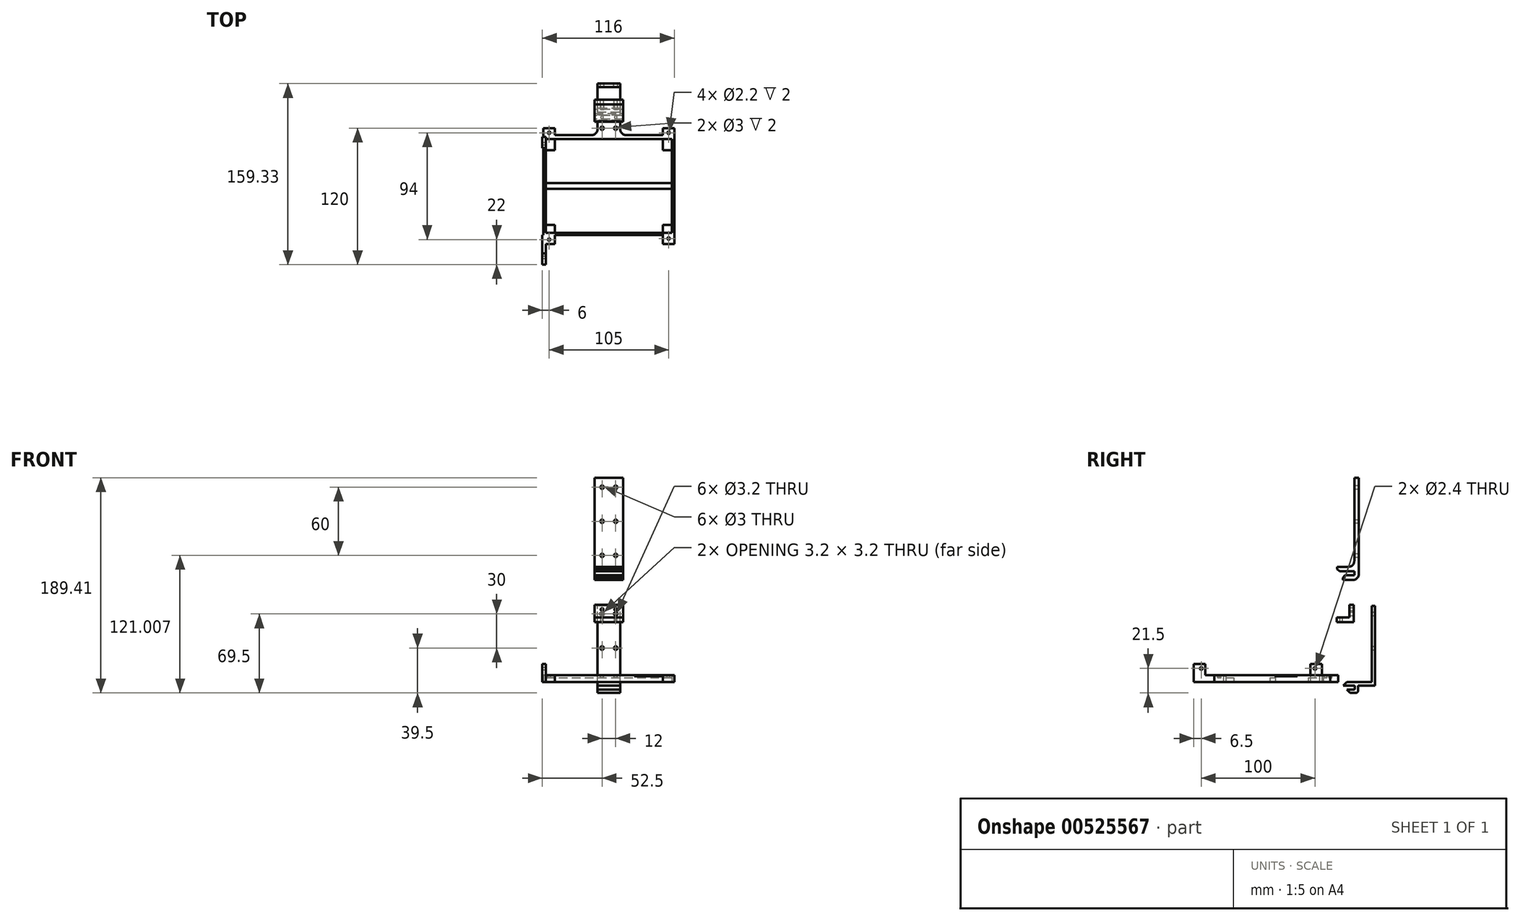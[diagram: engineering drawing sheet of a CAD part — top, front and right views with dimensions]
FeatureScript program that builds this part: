
annotation { "Feature Type Name" : "Feature", "Feature Type Description" : "" }
export const myFeature = defineFeature(function(context is Context, id is Id, definition is map)
    precondition{}
    {
        {
            var Q0;
            Q0=qCreatedBy(makeId("Top.planeOp"),FACE);
            var sketch = newSketch(context, id + "F0", { "sketchPlane" : qUnion([Q0])});
            skLineSegment(sketch, "E0.bottom", {"start": v(55.5, -41.25) * mm, "end": v(-55.5, -41.25) * mm});
            skLineSegment(sketch, "E0.top", {"start": v(55.5, 41.25) * mm, "end": v(-55.5, 41.25) * mm});
            skLineSegment(sketch, "E0.left", {"start": v(55.5, -41.25) * mm, "end": v(55.5, 41.25) * mm});
            skLineSegment(sketch, "E0.right", {"start": v(-55.5, -41.25) * mm, "end": v(-55.5, 41.25) * mm});
            skPoint(sketch, "E0.middle", {"position": v(0, 0) * mm});
            skLineSegment(sketch, "E1.bottom", {"start": v(57.5, -43.25) * mm, "end": v(-57.5, -43.25) * mm});
            skLineSegment(sketch, "E1.top", {"start": v(57.5, 43.25) * mm, "end": v(-57.5, 43.25) * mm});
            skLineSegment(sketch, "E1.left", {"start": v(57.5, -43.25) * mm, "end": v(57.5, 43.25) * mm});
            skLineSegment(sketch, "E1.right", {"start": v(-57.5, -43.25) * mm, "end": v(-57.5, 43.25) * mm});
            skSolve(sketch);
        }
        {
            var Q0;
            Q0=qSketchRegion(id+"F0",true);
            extrude(context, id + "F1", {"entities" : qUnion([Q0]), "depth" : 6 * mm, "offsetDistance" : 25 * mm});
        }
        {
            var Q0;
            Q0=makeQuery(id+"F1.opExtrude","CAP_FACE",FACE,{"disambiguationData":[OSD([sQuery(id+"F0.wireOp",EDGE,"E0.bottom"),sQuery(id+"F0.wireOp",EDGE,"E0.top"),sQuery(id+"F0.wireOp",EDGE,"E0.left"),sQuery(id+"F0.wireOp",EDGE,"E0.right"),sQuery(id+"F0.wireOp",EDGE,"E1.bottom"),sQuery(id+"F0.wireOp",EDGE,"E1.top"),sQuery(id+"F0.wireOp",EDGE,"E1.left"),sQuery(id+"F0.wireOp",EDGE,"E1.right")])],"isStart":true});
            var sketch = newSketch(context, id + "F2", { "sketchPlane" : qUnion([Q0])});
            skLineSegment(sketch, "E2.bottom", {"start": v(-55.5, -41.25) * mm, "end": v(-47.5, -41.25) * mm});
            skLineSegment(sketch, "E2.top", {"start": v(-55.5, -31.25) * mm, "end": v(-47.5, -31.25) * mm});
            skLineSegment(sketch, "E2.left", {"start": v(-55.5, -41.25) * mm, "end": v(-55.5, -31.25) * mm});
            skLineSegment(sketch, "E2.right", {"start": v(-47.5, -41.25) * mm, "end": v(-47.5, -31.25) * mm});
            skLineSegment(sketch, "E3.bottom", {"start": v(55.5, -41.25) * mm, "end": v(47.5, -41.25) * mm});
            skLineSegment(sketch, "E3.top", {"start": v(55.5, -31.25) * mm, "end": v(47.5, -31.25) * mm});
            skLineSegment(sketch, "E3.left", {"start": v(55.5, -41.25) * mm, "end": v(55.5, -31.25) * mm});
            skLineSegment(sketch, "E3.right", {"start": v(47.5, -41.25) * mm, "end": v(47.5, -31.25) * mm});
            skLineSegment(sketch, "E4.bottom", {"start": v(-55.5, 41.25) * mm, "end": v(-47.5, 41.25) * mm});
            skLineSegment(sketch, "E4.top", {"start": v(-55.5, 34.25) * mm, "end": v(-47.5, 34.25) * mm});
            skLineSegment(sketch, "E4.left", {"start": v(-55.5, 41.25) * mm, "end": v(-55.5, 34.25) * mm});
            skLineSegment(sketch, "E4.right", {"start": v(-47.5, 41.25) * mm, "end": v(-47.5, 34.25) * mm});
            skLineSegment(sketch, "E5.bottom", {"start": v(55.5, 41.25) * mm, "end": v(47.5, 41.25) * mm});
            skLineSegment(sketch, "E5.top", {"start": v(55.5, 34.25) * mm, "end": v(47.5, 34.25) * mm});
            skLineSegment(sketch, "E5.left", {"start": v(55.5, 41.25) * mm, "end": v(55.5, 34.25) * mm});
            skLineSegment(sketch, "E5.right", {"start": v(47.5, 41.25) * mm, "end": v(47.5, 34.25) * mm});
            skLineSegment(sketch, "E6.bottom", {"start": v(-55.5, -2.5) * mm, "end": v(55.5, -2.5) * mm});
            skLineSegment(sketch, "E6.top", {"start": v(-55.5, 2.5) * mm, "end": v(55.5, 2.5) * mm});
            skLineSegment(sketch, "E6.left", {"start": v(-55.5, -2.5) * mm, "end": v(-55.5, 2.5) * mm});
            skLineSegment(sketch, "E6.right", {"start": v(55.5, -2.5) * mm, "end": v(55.5, 2.5) * mm});
            skSolve(sketch);
        }
        {
            var Q0;
            Q0=qSketchRegion(id+"F2",true);
            extrude(context, id + "F3", {"entities" : qUnion([Q0]), "operationType" : NewBodyOperationType.ADD, "oppositeDirection" : true, "depth" : 4 * mm, "offsetDistance" : 25 * mm});
        }
        {
            var Q0;
            Q0=makeQuery(id+"F1.opExtrude","CAP_FACE",FACE,{"disambiguationData":[OSD([sQuery(id+"F0.wireOp",EDGE,"E0.bottom"),sQuery(id+"F0.wireOp",EDGE,"E0.top"),sQuery(id+"F0.wireOp",EDGE,"E0.left"),sQuery(id+"F0.wireOp",EDGE,"E0.right"),sQuery(id+"F0.wireOp",EDGE,"E1.bottom"),sQuery(id+"F0.wireOp",EDGE,"E1.top"),sQuery(id+"F0.wireOp",EDGE,"E1.left"),sQuery(id+"F0.wireOp",EDGE,"E1.right")])],"isStart":false});
            var sketch = newSketch(context, id + "F4", { "sketchPlane" : qUnion([Q0])});
            skLineSegment(sketch, "E7.bottom", {"start": v(22.5, -41.25) * mm, "end": v(47.5, -41.25) * mm});
            skLineSegment(sketch, "E7.top", {"start": v(22.5, -43.25) * mm, "end": v(47.5, -43.25) * mm});
            skLineSegment(sketch, "E7.left", {"start": v(22.5, -41.25) * mm, "end": v(22.5, -43.25) * mm});
            skLineSegment(sketch, "E7.right", {"start": v(47.5, -41.25) * mm, "end": v(47.5, -43.25) * mm});
            skLineSegment(sketch, "E8.bottom", {"start": v(57.5, 21.75) * mm, "end": v(55.5, 21.75) * mm});
            skLineSegment(sketch, "E8.top", {"start": v(57.5, 1.75) * mm, "end": v(55.5, 1.75) * mm});
            skLineSegment(sketch, "E8.left", {"start": v(57.5, 21.75) * mm, "end": v(57.5, 1.75) * mm});
            skLineSegment(sketch, "E8.right", {"start": v(55.5, 21.75) * mm, "end": v(55.5, 1.75) * mm});
            skSolve(sketch);
        }
        {
            var Q0;
            Q0=qSketchRegion(id+"F4",true);
            extrude(context, id + "F5", {"entities" : qUnion([Q0]), "operationType" : NewBodyOperationType.REMOVE, "oppositeDirection" : true, "depth" : 1 * mm, "offsetDistance" : 25 * mm});
        }
        {
            var Q0;
            Q0=makeQuery(id+"F3.boolean.opBoolean","MERGE",FACE,{"derivedFrom":[makeQuery(id+"F1.opExtrude","CAP_FACE",FACE,{"disambiguationData":[OSD([sQuery(id+"F0.wireOp",EDGE,"E0.bottom"),sQuery(id+"F0.wireOp",EDGE,"E0.top"),sQuery(id+"F0.wireOp",EDGE,"E0.left"),sQuery(id+"F0.wireOp",EDGE,"E0.right"),sQuery(id+"F0.wireOp",EDGE,"E1.bottom"),sQuery(id+"F0.wireOp",EDGE,"E1.top"),sQuery(id+"F0.wireOp",EDGE,"E1.left"),sQuery(id+"F0.wireOp",EDGE,"E1.right")])],"isStart":true}),makeQuery(id+"F3.opExtrude","CAP_FACE",FACE,{"disambiguationData":[OSD([sQuery(id+"F2.wireOp",EDGE,"E2.bottom"),sQuery(id+"F2.wireOp",EDGE,"E2.top"),sQuery(id+"F2.wireOp",EDGE,"E2.left"),sQuery(id+"F2.wireOp",EDGE,"E2.right")])],"isStart":true}),makeQuery(id+"F3.opExtrude","CAP_FACE",FACE,{"disambiguationData":[OSD([sQuery(id+"F2.wireOp",EDGE,"E3.bottom"),sQuery(id+"F2.wireOp",EDGE,"E3.top"),sQuery(id+"F2.wireOp",EDGE,"E3.left"),sQuery(id+"F2.wireOp",EDGE,"E3.right")])],"isStart":true}),makeQuery(id+"F3.opExtrude","CAP_FACE",FACE,{"disambiguationData":[OSD([sQuery(id+"F2.wireOp",EDGE,"E4.bottom"),sQuery(id+"F2.wireOp",EDGE,"E4.top"),sQuery(id+"F2.wireOp",EDGE,"E4.left"),sQuery(id+"F2.wireOp",EDGE,"E4.right")])],"isStart":true}),makeQuery(id+"F3.opExtrude","CAP_FACE",FACE,{"disambiguationData":[OSD([sQuery(id+"F2.wireOp",EDGE,"E5.bottom"),sQuery(id+"F2.wireOp",EDGE,"E5.top"),sQuery(id+"F2.wireOp",EDGE,"E5.left"),sQuery(id+"F2.wireOp",EDGE,"E5.right")])],"isStart":true})]});
            var sketch = newSketch(context, id + "F6", { "sketchPlane" : qUnion([Q0])});
            skLineSegment(sketch, "E9.bottom", {"start": v(10, -57.75) * mm, "end": v(-10, -57.75) * mm});
            skLineSegment(sketch, "E9.top", {"start": v(10, -44.75) * mm, "end": v(-10, -44.75) * mm});
            skLineSegment(sketch, "E9.left", {"start": v(10, -57.75) * mm, "end": v(10, -44.75) * mm});
            skLineSegment(sketch, "E9.right", {"start": v(-10, -57.75) * mm, "end": v(-10, -44.75) * mm});
            skPoint(sketch, "E9.middle", {"position": v(0, -51.25) * mm});
            skCircle(sketch, "E10", {"center": v(-6, -50.75) * mm, "radius": 1.5 * mm, "construction": true});
            skCircle(sketch, "E11", {"center": v(6, -50.75) * mm, "radius": 1.5 * mm, "construction": true});
            skLineSegment(sketch, "E12.bottom", {"start": v(-57.5, -43.25) * mm, "end": v(57.5, -43.25) * mm});
            skLineSegment(sketch, "E12.top", {"start": v(-57.5, -44.75) * mm, "end": v(57.5, -44.75) * mm});
            skLineSegment(sketch, "E12.left", {"start": v(-57.5, -43.25) * mm, "end": v(-57.5, -44.75) * mm});
            skLineSegment(sketch, "E12.right", {"start": v(57.5, -43.25) * mm, "end": v(57.5, -44.75) * mm});
            skSolve(sketch);
        }
        {
            var Q0;
            Q0 = qSketchRegion(id + "F6", true);
            extrude(context, id + "F7", {"entities" : qUnion([Q0]), "operationType" : NewBodyOperationType.ADD, "oppositeDirection" : true, "depth" : 6 * mm, "offsetDistance" : 25 * mm});
        }
        {
            var Q0;
            Q0=qCreatedBy(makeId("Top.planeOp"),FACE);
            var sketch = newSketch(context, id + "F8", { "sketchPlane" : qUnion([Q0])});
            skLineSegment(sketch, "E13.bottom", {"start": v(10, 75.08) * mm, "end": v(-10, 75.08) * mm});
            skLineSegment(sketch, "E13.top", {"start": v(10, 87.08) * mm, "end": v(-10, 87.08) * mm});
            skLineSegment(sketch, "E13.left", {"start": v(10, 75.08) * mm, "end": v(10, 87.08) * mm});
            skLineSegment(sketch, "E13.right", {"start": v(-10, 75.08) * mm, "end": v(-10, 87.08) * mm});
            skPoint(sketch, "E13.middle", {"position": v(0, 81.08) * mm});
            skCircle(sketch, "E14", {"center": v(-6, 81.08) * mm, "radius": 1.2 * mm, "construction": true});
            skCircle(sketch, "E15", {"center": v(6, 81.08) * mm, "radius": 1.2 * mm, "construction": true});
            skSolve(sketch);
        }
        {
            var Q0;
            Q0 = qSketchRegion(id + "F8", true);
            extrude(context, id + "F9", {"entities" : qUnion([Q0]), "oppositeDirection" : true, "depth" : 3 * mm, "offsetDistance" : 25 * mm});
        }
        {
            var Q0;
            Q0=makeQuery(id+"F9.opExtrude","SWEPT_FACE",FACE,{"disambiguationData":[OSD([sQuery(id+"F8.wireOp",EDGE,"E13.right")])]});
            var sketch = newSketch(context, id + "F10", { "sketchPlane" : qUnion([Q0])});
            skLineSegment(sketch, "E16", {"start": v(-75.08, -3) * mm, "end": v(-75.08, -9.5) * mm});
            skLineSegment(sketch, "E17", {"start": v(-75.08, -9.5) * mm, "end": v(-65.08, -9.5) * mm});
            skLineSegment(sketch, "E18", {"start": v(-65.08, -9.5) * mm, "end": v(-65.08, -6.5) * mm});
            skLineSegment(sketch, "E19", {"start": v(-65.08, -6.5) * mm, "end": v(-71.58, -6.5) * mm});
            skLineSegment(sketch, "E20", {"start": v(-72.08, -6) * mm, "end": v(-72.08, -3.5) * mm});
            skLineSegment(sketch, "E21", {"start": v(-71.58, -3) * mm, "end": v(-62.08, -3) * mm});
            skLineSegment(sketch, "E22", {"start": v(-62.08, -3) * mm, "end": v(-62.08, 0) * mm});
            skLineSegment(sketch, "E23", {"start": v(-62.08, 0) * mm, "end": v(-75.08, 0) * mm});
            skLineSegment(sketch, "E24", {"start": v(-75.08, 0) * mm, "end": v(-75.08, -3) * mm});
            skPoint(sketch, "E25.visualSharp", {"position": v(-72.08, -3) * mm});
            skArc(sketch, "E25.filletArc", {"start": v(-71.58, -3) * mm, "mid": v(-71.94, -3.15) * mm, "end": v(-72.08, -3.5) * mm});
            skPoint(sketch, "E26.visualSharp", {"position": v(-72.08, -6.5) * mm});
            skArc(sketch, "E26.filletArc", {"start": v(-72.08, -6) * mm, "mid": v(-71.94, -6.35) * mm, "end": v(-71.58, -6.5) * mm});
            skLineSegment(sketch, "E27.bottom", {"start": v(-87.08, -3) * mm, "end": v(-90.08, -3) * mm});
            skLineSegment(sketch, "E27.top", {"start": v(-87.08, 67) * mm, "end": v(-90.08, 67) * mm});
            skLineSegment(sketch, "E27.left", {"start": v(-87.08, -3) * mm, "end": v(-87.08, 67) * mm});
            skLineSegment(sketch, "E27.right", {"start": v(-90.08, -3) * mm, "end": v(-90.08, 67) * mm});
            skSolve(sketch);
        }
        {
            var Q0;
            Q0 = qSketchRegion(id + "F10", true);
            extrude(context, id + "F11", {"entities" : qUnion([Q0]), "operationType" : NewBodyOperationType.ADD, "oppositeDirection" : true, "depth" : 20 * mm, "offsetDistance" : 25 * mm});
        }
        {
            var Q0;
            Q0=qCreatedBy(makeId("Top.planeOp"),FACE);
            var sketch = newSketch(context, id + "F12", { "sketchPlane" : qUnion([Q0])});
            skLineSegment(sketch, "E28.bottom", {"start": v(-58.5, 43.25) * mm, "end": v(-55.5, 43.25) * mm});
            skLineSegment(sketch, "E28.top", {"start": v(-58.5, 33.25) * mm, "end": v(-55.5, 33.25) * mm});
            skLineSegment(sketch, "E28.left", {"start": v(-58.5, 43.25) * mm, "end": v(-58.5, 33.25) * mm});
            skLineSegment(sketch, "E28.right", {"start": v(-55.5, 43.25) * mm, "end": v(-55.5, 33.25) * mm});
            skLineSegment(sketch, "E29.bottom", {"start": v(-55.5, -43.25) * mm, "end": v(-58.5, -43.25) * mm});
            skLineSegment(sketch, "E29.top", {"start": v(-55.5, -69.25) * mm, "end": v(-58.5, -69.25) * mm});
            skLineSegment(sketch, "E29.left", {"start": v(-55.5, -43.25) * mm, "end": v(-55.5, -69.25) * mm});
            skLineSegment(sketch, "E29.right", {"start": v(-58.5, -43.25) * mm, "end": v(-58.5, -69.25) * mm});
            skSolve(sketch);
        }
        {
            var Q0;
            Q0 = qSketchRegion(id + "F12", true);
            extrude(context, id + "F13", {"entities" : qUnion([Q0]), "operationType" : NewBodyOperationType.ADD, "depth" : 16 * mm, "offsetDistance" : 25 * mm});
        }
        {
            var Q0;
            Q0=makeQuery(id+"F11.opExtrude","SWEPT_EDGE",EDGE,{"disambiguationData":[OSD([sQuery(id+"F10.wireOp",EDGE,"E22"),sQuery(id+"F10.wireOp",EDGE,"E23")])]});
            var Q1;
            Q1=makeQuery(id+"F11.opExtrude","SWEPT_EDGE",EDGE,{"disambiguationData":[OSD([sQuery(id+"F10.wireOp",EDGE,"E17"),sQuery(id+"F10.wireOp",EDGE,"E18")])]});
            chamfer(context, id + "F14", {"entities" : qUnion([Q0, Q1]), "width" : 3 * mm, "tangentPropagation" : true});
        }
        {
            var Q0;
            Q0=makeQuery(id+"F13.opExtrude","SWEPT_FACE",FACE,{"disambiguationData":[OSD([sQuery(id+"F12.wireOp",EDGE,"E29.left")])]});
            var sketch = newSketch(context, id + "F15", { "sketchPlane" : qUnion([Q0])});
            skLineSegment(sketch, "E30.bottom", {"start": v(-43.25, 16) * mm, "end": v(-59.25, 16) * mm});
            skLineSegment(sketch, "E30.top", {"start": v(-43.25, 6) * mm, "end": v(-59.25, 6) * mm});
            skLineSegment(sketch, "E30.left", {"start": v(-43.25, 16) * mm, "end": v(-43.25, 6) * mm});
            skLineSegment(sketch, "E30.right", {"start": v(-59.25, 16) * mm, "end": v(-59.25, 6) * mm});
            skCircle(sketch, "E31", {"center": v(-62.75, 12) * mm, "radius": 1.2 * mm});
            skCircle(sketch, "E32", {"center": v(37.25, 12) * mm, "radius": 1.2 * mm});
            skSolve(sketch);
        }
        {
            var Q0;
            Q0 = qSketchRegion(id + "F15", true);
            extrude(context, id + "F16", {"entities" : qUnion([Q0]), "operationType" : NewBodyOperationType.REMOVE, "oppositeDirection" : true, "depth" : 25 * mm, "offsetDistance" : 25 * mm});
        }
        {
            var Q0;
            Q0=makeQuery(id+"F9.opExtrude","CAP_EDGE",EDGE,{"disambiguationData":[OSD([sQuery(id+"F8.wireOp",EDGE,"E13.bottom")])],"isStart":false});
            var Q1;
            Q1=makeQuery(id+"F11.opExtrude","SWEPT_EDGE",EDGE,{"disambiguationData":[OSD([sQuery(id+"F10.wireOp",EDGE,"E16"),sQuery(id+"F10.wireOp",EDGE,"E17")])]});
            fillet(context, id + "F17", {"entities" : qUnion([Q0, Q1]), "radius" : 2 * mm, "tangentPropagation" : true, "allowEdgeOverflow" : false});
        }
        {
            var Q0;
            Q0=qCreatedBy(makeId("Right.planeOp"),FACE);
            var sketch = newSketch(context, id + "F18", { "sketchPlane" : qUnion([Q0])});
            skLineSegment(sketch, "E33.bottom", {"start": v(56.38, 56.93) * mm, "end": v(71.38, 56.93) * mm});
            skLineSegment(sketch, "E33.top", {"start": v(56.38, 52.93) * mm, "end": v(71.38, 52.93) * mm});
            skLineSegment(sketch, "E33.left", {"start": v(56.38, 56.93) * mm, "end": v(56.38, 52.93) * mm});
            skLineSegment(sketch, "E33.right", {"start": v(71.38, 56.93) * mm, "end": v(71.38, 52.93) * mm});
            skLineSegment(sketch, "E34.bottom", {"start": v(71.38, 56.93) * mm, "end": v(67.38, 56.93) * mm});
            skLineSegment(sketch, "E34.top", {"start": v(71.38, 67.93) * mm, "end": v(67.38, 67.93) * mm});
            skLineSegment(sketch, "E34.left", {"start": v(71.38, 56.93) * mm, "end": v(71.38, 67.93) * mm});
            skLineSegment(sketch, "E34.right", {"start": v(67.38, 56.93) * mm, "end": v(67.38, 67.93) * mm});
            skSolve(sketch);
        }
        {
            var Q0;
            Q0 = qSketchRegion(id + "F18", true);
            extrude(context, id + "F19", {"entities" : qUnion([Q0]), "endBound" : BoundingType.SYMMETRIC, "depth" : 25 * mm, "offsetDistance" : 25 * mm});
        }
        {
            var Q0;
            Q0=makeQuery(id+"F19.opExtrude","SWEPT_FACE",FACE,{"disambiguationData":[OSD([sQuery(id+"F18.wireOp",EDGE,"E33.bottom")])]});
            var sketch = newSketch(context, id + "F20", { "sketchPlane" : qUnion([Q0])});
            skCircle(sketch, "E35", {"center": v(-6, 60.38) * mm, "radius": 1.2 * mm});
            skCircle(sketch, "E36", {"center": v(6, 60.38) * mm, "radius": 1.2 * mm});
            skSolve(sketch);
        }
        {
            var Q0;
            Q0=makeQuery(id+"F19.opExtrude","SWEPT_FACE",FACE,{"disambiguationData":[OSD([sQuery(id+"F18.wireOp",EDGE,"E34.right")])]});
            var sketch = newSketch(context, id + "F21", { "sketchPlane" : qUnion([Q0])});
            skCircle(sketch, "E37", {"center": v(-6, 63.93) * mm, "radius": 1.2 * mm});
            skCircle(sketch, "E38", {"center": v(6, 63.93) * mm, "radius": 1.2 * mm});
            skSolve(sketch);
        }
        {
            var Q0;
            Q0=sQuery(id+"F20.wireOp",VERTEX,"E35.center");
            var Q1;
            Q1=sQuery(id+"F20.wireOp",VERTEX,"E36.center");
            var Q2;
            Q2=sQuery(id+"F21.wireOp",VERTEX,"E37.center");
            var Q3;
            Q3=sQuery(id+"F21.wireOp",VERTEX,"E38.center");
            var Q4;
            Q4=makeQuery(id+"F19.opExtrude","SWEPT_BODY",BODY,{"disambiguationData":[OSD([sQuery(id+"F18.wireOp",EDGE,"E33.bottom"),sQuery(id+"F18.wireOp",EDGE,"E33.top"),sQuery(id+"F18.wireOp",EDGE,"E33.left"),sQuery(id+"F18.wireOp",EDGE,"E33.right"),sQuery(id+"F18.wireOp",EDGE,"E34.top"),sQuery(id+"F18.wireOp",EDGE,"E34.left"),sQuery(id+"F18.wireOp",EDGE,"E34.right")])]});
            hole(context, id + "F22", {"style" : HoleStyle.SIMPLE, "endStyle" : HoleEndStyle.BLIND, "holeDiameter" : 2.4 * mm, "majorDiameter" : 5 * mm, "holeDepth" : 5 * mm, "tappedDepth" : 12 * mm, "tapClearance" : 3, "locations" : qUnion([Q0, Q1, Q2, Q3]), "scope" : qUnion([Q4])});
        }
        {
            var Q0;
            Q0=makeQuery(id+"F11.opExtrude","SWEPT_FACE",FACE,{"disambiguationData":[OSD([sQuery(id+"F10.wireOp",EDGE,"E27.right")])]});
            var sketch = newSketch(context, id + "F23", { "sketchPlane" : qUnion([Q0])});
            skCircle(sketch, "E39", {"center": v(-6, 30) * mm, "radius": 1.6 * mm});
            skCircle(sketch, "E40", {"center": v(6, 30) * mm, "radius": 1.6 * mm});
            skCircle(sketch, "E41", {"center": v(-6, 60) * mm, "radius": 1.6 * mm});
            skCircle(sketch, "E42", {"center": v(6, 60) * mm, "radius": 1.6 * mm});
            skSolve(sketch);
        }
        {
            var Q0;
            Q0 = qSketchRegion(id + "F23", true);
            extrude(context, id + "F24", {"entities" : qUnion([Q0]), "operationType" : NewBodyOperationType.REMOVE, "oppositeDirection" : true, "depth" : 25 * mm, "offsetDistance" : 25 * mm});
        }
        {
            var Q0;
            Q0=qCreatedBy(makeId("Right.planeOp"),FACE);
            var sketch = newSketch(context, id + "F25", { "sketchPlane" : qUnion([Q0])});
            skLineSegment(sketch, "E43", {"start": v(61.75, 89.9) * mm, "end": v(75.75, 89.9) * mm});
            skLineSegment(sketch, "E44", {"start": v(75.75, 89.9) * mm, "end": v(75.75, 179.9) * mm});
            skLineSegment(sketch, "E45", {"start": v(75.75, 179.9) * mm, "end": v(71.75, 179.9) * mm});
            skLineSegment(sketch, "E46", {"start": v(71.75, 179.9) * mm, "end": v(71.75, 101.5) * mm});
            skLineSegment(sketch, "E47", {"start": v(71.75, 101.5) * mm, "end": v(56.75, 101.5) * mm});
            skLineSegment(sketch, "E48", {"start": v(56.75, 101.5) * mm, "end": v(56.75, 97.5) * mm});
            skLineSegment(sketch, "E49", {"start": v(56.75, 97.5) * mm, "end": v(71.75, 97.5) * mm});
            skLineSegment(sketch, "E50", {"start": v(71.75, 97.5) * mm, "end": v(71.75, 93.9) * mm});
            skLineSegment(sketch, "E51", {"start": v(71.75, 93.9) * mm, "end": v(61.75, 93.9) * mm});
            skLineSegment(sketch, "E52", {"start": v(61.75, 93.9) * mm, "end": v(61.75, 89.9) * mm});
            skSolve(sketch);
        }
        {
            var Q0;
            Q0 = qSketchRegion(id + "F25", true);
            extrude(context, id + "F26", {"entities" : qUnion([Q0]), "endBound" : BoundingType.SYMMETRIC, "depth" : 25 * mm, "offsetDistance" : 25 * mm});
        }
        {
            var Q0;
            Q0=makeQuery(id+"F26.opExtrude","SWEPT_EDGE",EDGE,{"disambiguationData":[OSD([sQuery(id+"F25.wireOp",EDGE,"E46"),sQuery(id+"F25.wireOp",EDGE,"E47")])]});
            var Q1;
            Q1=makeQuery(id+"F26.opExtrude","SWEPT_EDGE",EDGE,{"disambiguationData":[OSD([sQuery(id+"F25.wireOp",EDGE,"E43"),sQuery(id+"F25.wireOp",EDGE,"E44")])]});
            var Q2;
            Q2=makeQuery(id+"F7.opExtrude","SWEPT_EDGE",EDGE,{"disambiguationData":[OSD([sQuery(id+"F6.wireOp",EDGE,"E9.right"),sQuery(id+"F6.wireOp",EDGE,"E12.top")])]});
            var Q3;
            Q3=makeQuery(id+"F7.opExtrude","SWEPT_EDGE",EDGE,{"disambiguationData":[OSD([sQuery(id+"F6.wireOp",EDGE,"E9.left"),sQuery(id+"F6.wireOp",EDGE,"E12.top")])]});
            fillet(context, id + "F27", {"entities" : qUnion([Q0, Q1, Q2, Q3]), "radius" : 5 * mm, "tangentPropagation" : true, "allowEdgeOverflow" : false});
        }
        {
            var Q0;
            Q0=makeQuery(id+"F26.opExtrude","SWEPT_EDGE",EDGE,{"disambiguationData":[OSD([sQuery(id+"F25.wireOp",EDGE,"E48"),sQuery(id+"F25.wireOp",EDGE,"E49")])]});
            var Q1;
            Q1=makeQuery(id+"F26.opExtrude","SWEPT_EDGE",EDGE,{"disambiguationData":[OSD([sQuery(id+"F25.wireOp",EDGE,"E51"),sQuery(id+"F25.wireOp",EDGE,"E52")])]});
            chamfer(context, id + "F28", {"entities" : qUnion([Q0, Q1]), "width" : 2 * mm, "tangentPropagation" : true});
        }
        {
            var Q0;
            Q0=makeQuery(id+"F26.opExtrude","SWEPT_FACE",FACE,{"disambiguationData":[OSD([sQuery(id+"F25.wireOp",EDGE,"E44")])]});
            var sketch = newSketch(context, id + "F29", { "sketchPlane" : qUnion([Q0])});
            skCircle(sketch, "E53", {"center": v(6, 111.5) * mm, "radius": 1.5 * mm});
            skCircle(sketch, "E54", {"center": v(-6, 111.5) * mm, "radius": 1.5 * mm});
            skCircle(sketch, "E55.0.1.0", {"center": v(6, 141.5) * mm, "radius": 1.5 * mm});
            skCircle(sketch, "E55.0.1.1", {"center": v(-6, 141.5) * mm, "radius": 1.5 * mm});
            skCircle(sketch, "E55.0.2.0", {"center": v(6, 171.5) * mm, "radius": 1.5 * mm});
            skCircle(sketch, "E55.0.2.1", {"center": v(-6, 171.5) * mm, "radius": 1.5 * mm});
            skLineSegment(sketch, "E55.direction1", {"start": v(-6, 111.5) * mm, "end": v(19, 111.5) * mm, "construction": true});
            skLineSegment(sketch, "E55.direction2", {"start": v(-6, 111.5) * mm, "end": v(-6, 141.5) * mm, "construction": true});
            skSolve(sketch);
        }
        {
            var Q0;
            Q0 = qSketchRegion(id + "F29", true);
            extrude(context, id + "F30", {"entities" : qUnion([Q0]), "operationType" : NewBodyOperationType.REMOVE, "oppositeDirection" : true, "depth" : 25 * mm, "offsetDistance" : 25 * mm});
        }
        {
            var Q0;
            Q0=qCreatedBy(makeId("Top.planeOp"),FACE);
            var sketch = newSketch(context, id + "F31", { "sketchPlane" : qUnion([Q0])});
            skLineSegment(sketch, "E56.3", {"start": v(-57.5, 44.75) * mm, "end": v(-15, 44.75) * mm});
            skLineSegment(sketch, "E56.4", {"start": v(15, 44.75) * mm, "end": v(57.5, 44.75) * mm});
            skLineSegment(sketch, "E57.bottom", {"start": v(57.5, -43.25) * mm, "end": v(47.5, -43.25) * mm});
            skLineSegment(sketch, "E57.top", {"start": v(57.5, -51.25) * mm, "end": v(47.5, -51.25) * mm});
            skLineSegment(sketch, "E57.left", {"start": v(57.5, -43.25) * mm, "end": v(57.5, -51.25) * mm});
            skLineSegment(sketch, "E57.right", {"start": v(47.5, -43.25) * mm, "end": v(47.5, -51.25) * mm});
            skLineSegment(sketch, "E58.0", {"start": v(57.5, -43.25) * mm, "end": v(-55.5, -43.25) * mm});
            skLineSegment(sketch, "E58.1", {"start": v(-55.5, -43.25) * mm, "end": v(-55.5, -69.25) * mm});
            skLineSegment(sketch, "E59.bottom", {"start": v(-55.5, -43.25) * mm, "end": v(-47.5, -43.25) * mm});
            skLineSegment(sketch, "E59.top", {"start": v(-55.5, -51.25) * mm, "end": v(-47.5, -51.25) * mm});
            skLineSegment(sketch, "E59.left", {"start": v(-55.5, -43.25) * mm, "end": v(-55.5, -51.25) * mm});
            skLineSegment(sketch, "E59.right", {"start": v(-47.5, -43.25) * mm, "end": v(-47.5, -51.25) * mm});
            skLineSegment(sketch, "E60.bottom", {"start": v(-57.5, 44.75) * mm, "end": v(-47.5, 44.75) * mm});
            skLineSegment(sketch, "E60.top", {"start": v(-57.5, 50.75) * mm, "end": v(-47.5, 50.75) * mm});
            skLineSegment(sketch, "E60.left", {"start": v(-57.5, 44.75) * mm, "end": v(-57.5, 50.75) * mm});
            skLineSegment(sketch, "E60.right", {"start": v(-47.5, 44.75) * mm, "end": v(-47.5, 50.75) * mm});
            skLineSegment(sketch, "E61.bottom", {"start": v(57.5, 44.75) * mm, "end": v(47.5, 44.75) * mm});
            skLineSegment(sketch, "E61.top", {"start": v(57.5, 50.75) * mm, "end": v(47.5, 50.75) * mm});
            skLineSegment(sketch, "E61.left", {"start": v(57.5, 44.75) * mm, "end": v(57.5, 50.75) * mm});
            skLineSegment(sketch, "E61.right", {"start": v(47.5, 44.75) * mm, "end": v(47.5, 50.75) * mm});
            skPoint(sketch, "E62", {"position": v(52.5, -47.25) * mm});
            skPoint(sketch, "E62.positionSnap0", {"position": v(52.5, -43.25) * mm});
            skPoint(sketch, "E62.positionSnap1", {"position": v(47.5, -47.25) * mm});
            skPoint(sketch, "E63", {"position": v(-51.5, -47.25) * mm});
            skPoint(sketch, "E63.positionSnap0", {"position": v(-47.5, -47.25) * mm});
            skPoint(sketch, "E63.positionSnap1", {"position": v(-51.5, -43.25) * mm});
            skPoint(sketch, "E64", {"position": v(-52.5, 46.75) * mm});
            skPoint(sketch, "E64.positionSnap0", {"position": v(-52.5, 50.75) * mm});
            skPoint(sketch, "E65", {"position": v(52.5, 46.75) * mm});
            skPoint(sketch, "E65.positionSnap0", {"position": v(52.5, 50.75) * mm});
            skSolve(sketch);
        }
        {
            var Q0;
            Q0 = qSketchRegion(id + "F31", true);
            extrude(context, id + "F32", {"entities" : qUnion([Q0]), "operationType" : NewBodyOperationType.ADD, "depth" : 6 * mm, "offsetDistance" : 25 * mm});
        }
        {
            var Q0;
            {var subQ0=sQuery(id+"F6.wireOp",EDGE,"E9.bottom");var subQ2=sQuery(id+"F0.wireOp",EDGE,"E1.right");var subQ4=sQuery(id+"F6.wireOp",EDGE,"E9.left");var subQ5=sQuery(id+"F0.wireOp",EDGE,"E0.top");var subQ6=makeQuery(id+"F1.opExtrude","SWEPT_FACE",FACE,{"disambiguationData":[OSD([subQ5])]});var subQ7=sQuery(id+"F0.wireOp",EDGE,"E1.left");var subQ9=sQuery(id+"F6.wireOp",EDGE,"E9.right");var subQ10=sQuery(id+"F0.wireOp",EDGE,"E0.left");var subQ12=sQuery(id+"F6.wireOp",EDGE,"E10");var subQ13=sQuery(id+"F0.wireOp",EDGE,"E0.right");var subQ15=sQuery(id+"F6.wireOp",EDGE,"E11");var subQ16=sQuery(id+"F6.wireOp",EDGE,"E12.top");var subQ17=sQuery(id+"F6.wireOp",EDGE,"E12.left");var subQ18=sQuery(id+"F6.wireOp",EDGE,"E12.right");var subQ19=sQuery(id+"F0.wireOp",EDGE,"E0.bottom");var subQ20=sQuery(id+"F0.wireOp",EDGE,"E1.bottom");var subQ21=sQuery(id+"F0.wireOp",EDGE,"E1.top");Q0=makeQuery(id+"F32.boolean.opBoolean","MERGE",FACE,{"derivedFrom":[makeQuery(id+"F13.boolean.opBoolean","SPLIT",FACE,{"disambiguationData":[TD([subQ6])],"derivedFrom":makeQuery(id+"F7.boolean.opBoolean","MERGE",FACE,{"derivedFrom":[makeQuery(id+"F5.boolean.opBoolean","SPLIT",FACE,{"disambiguationData":[TD([subQ6])],"derivedFrom":makeQuery(id+"F1.opExtrude","CAP_FACE",FACE,{"disambiguationData":[OSD([subQ19,subQ5,subQ10,subQ13,subQ20,subQ21,subQ7,subQ2])],"isStart":false})}),makeQuery(id+"F7.opExtrude","CAP_FACE",FACE,{"disambiguationData":[OSD([subQ0,subQ4,subQ9,subQ12,subQ15,sQuery(id+"F6.wireOp",EDGE,"E12.bottom"),subQ16,subQ17,subQ18])],"isStart":false})]})}),makeQuery(id+"F32.opExtrude","CAP_FACE",FACE,{"disambiguationData":[OSD([sQuery(id+"F31.wireOp",EDGE,"E60.bottom"),sQuery(id+"F31.wireOp",EDGE,"E60.top"),sQuery(id+"F31.wireOp",EDGE,"E60.left"),sQuery(id+"F31.wireOp",EDGE,"E60.right")])],"isStart":false}),makeQuery(id+"F32.opExtrude","CAP_FACE",FACE,{"disambiguationData":[OSD([sQuery(id+"F31.wireOp",EDGE,"E61.bottom"),sQuery(id+"F31.wireOp",EDGE,"E61.top"),sQuery(id+"F31.wireOp",EDGE,"E61.left"),sQuery(id+"F31.wireOp",EDGE,"E61.right")])],"isStart":false})]});}
            var sketch = newSketch(context, id + "F33", { "sketchPlane" : qUnion([Q0])});
            skCircle(sketch, "E66", {"center": v(-52.5, 46.75) * mm, "radius": 1.1 * mm});
            skPoint(sketch, "E66.centerSnap0", {"position": v(-52.5, 50.75) * mm});
            skCircle(sketch, "E67", {"center": v(52.5, 46.75) * mm, "radius": 1.1 * mm});
            skPoint(sketch, "E67.centerSnap0", {"position": v(52.5, 50.75) * mm});
            skLineSegment(sketch, "E68.0", {"start": v(-55.5, -51.25) * mm, "end": v(-47.5, -51.25) * mm});
            skLineSegment(sketch, "E68.1", {"start": v(-47.5, -43.25) * mm, "end": v(-47.5, -51.25) * mm});
            skLineSegment(sketch, "E68.2", {"start": v(57.5, -51.25) * mm, "end": v(47.5, -51.25) * mm});
            skLineSegment(sketch, "E68.3", {"start": v(47.5, -41.25) * mm, "end": v(47.5, -51.25) * mm});
            skCircle(sketch, "E69", {"center": v(-52.5, -47.25) * mm, "radius": 1.1 * mm});
            skPoint(sketch, "E69.centerSnap0", {"position": v(-47.5, -47.25) * mm});
            skCircle(sketch, "E70", {"center": v(52.5, -46.25) * mm, "radius": 1.1 * mm});
            skPoint(sketch, "E70.centerSnap0", {"position": v(47.5, -46.25) * mm});
            skPoint(sketch, "E70.centerSnap1", {"position": v(52.5, -51.25) * mm});
            skCircle(sketch, "E71", {"center": v(-6, 50.75) * mm, "radius": 1.5 * mm});
            skCircle(sketch, "E72", {"center": v(6, 50.75) * mm, "radius": 1.5 * mm});
            skSolve(sketch);
        }
        {
            var Q0;
            Q0 = qSketchRegion(id + "F33", true);
            extrude(context, id + "F34", {"entities" : qUnion([Q0]), "operationType" : NewBodyOperationType.REMOVE, "oppositeDirection" : true, "depth" : 2 * mm, "offsetDistance" : 25 * mm});
        }
    });
